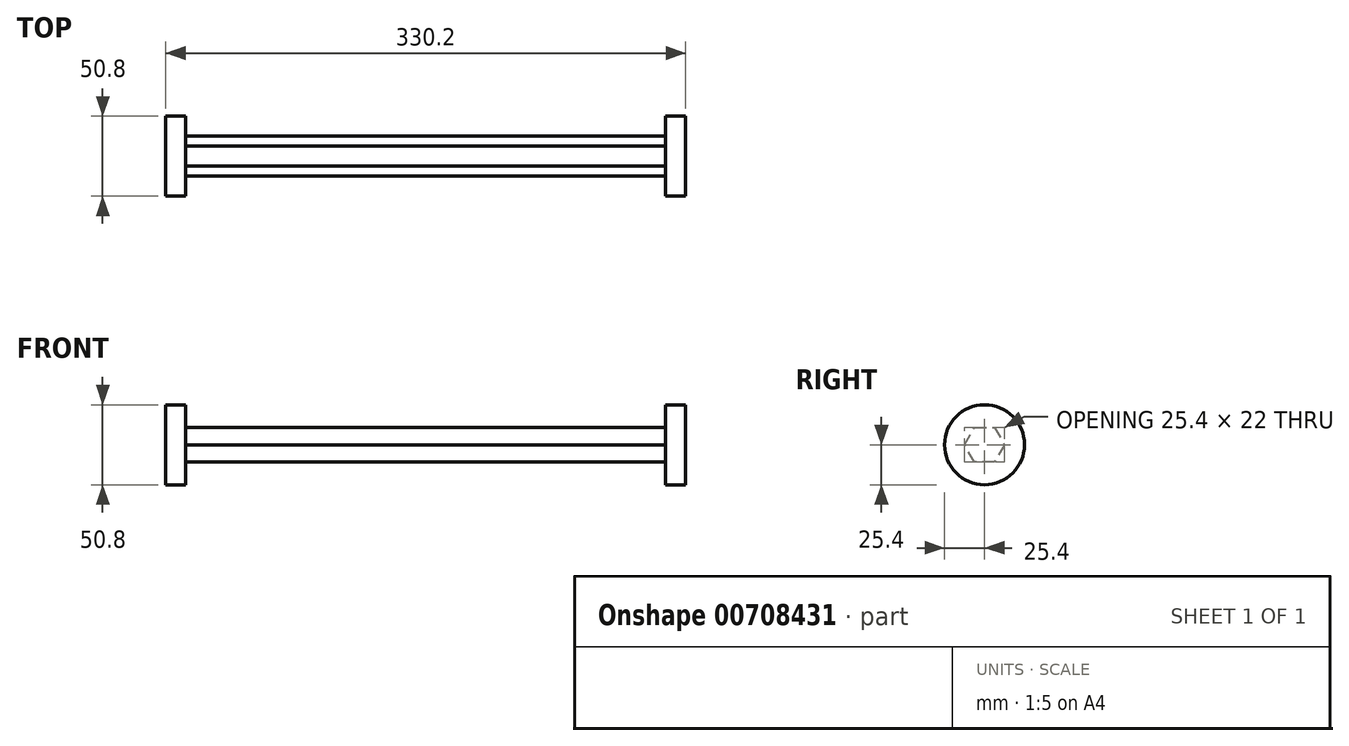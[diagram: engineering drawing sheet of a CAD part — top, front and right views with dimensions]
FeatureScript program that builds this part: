
annotation { "Feature Type Name" : "Feature", "Feature Type Description" : "" }
export const myFeature = defineFeature(function(context is Context, id is Id, definition is map)
    precondition{}
    {
        {
            var Q0;
            Q0=qCreatedBy(makeId("Right.planeOp"),FACE);
            var sketch = newSketch(context, id + "F0", { "sketchPlane" : qUnion([Q0])});
            skCircle(sketch, "E0.cCircle", {"center": v(0, 0) * mm, "radius": 12.7 * mm, "construction": true});
            skLineSegment(sketch, "E0.0", {"start": v(12.7, 0) * mm, "end": v(6.35, -11) * mm});
            skLineSegment(sketch, "E0.1", {"start": v(6.35, -11) * mm, "end": v(-6.35, -11) * mm});
            skLineSegment(sketch, "E0.2", {"start": v(-6.35, -11) * mm, "end": v(-12.7, 0) * mm});
            skLineSegment(sketch, "E0.3", {"start": v(-12.7, 0) * mm, "end": v(-6.35, 11) * mm});
            skLineSegment(sketch, "E0.4", {"start": v(-6.35, 11) * mm, "end": v(6.35, 11) * mm});
            skLineSegment(sketch, "E0.5", {"start": v(6.35, 11) * mm, "end": v(12.7, 0) * mm});
            skSolve(sketch);
        }
        {
            var Q0;
            Q0=makeQuery(id+"F0.imprint","IMPRINT",FACE,{"disambiguationData":[TD([[makeQuery(id+"F0.imprint","IMPRINT",EDGE,{"derivedFrom":sQuery(id+"F0.wireOp",EDGE,"E0.0")}),-1.0]])]});
            extrude(context, id + "F1", {"entities" : qUnion([Q0]), "depth" : 304.8 * mm, "offsetDistance" : 25.4 * mm});
        }
        {
            var Q0;
            Q0=makeQuery(id+"F1.opExtrude","CAP_FACE",FACE,{"disambiguationData":[OSD([sQuery(id+"F0.wireOp",EDGE,"E0.0"),sQuery(id+"F0.wireOp",EDGE,"E0.1"),sQuery(id+"F0.wireOp",EDGE,"E0.2"),sQuery(id+"F0.wireOp",EDGE,"E0.3"),sQuery(id+"F0.wireOp",EDGE,"E0.4"),sQuery(id+"F0.wireOp",EDGE,"E0.5")])],"isStart":false});
            var sketch = newSketch(context, id + "F2", { "sketchPlane" : qUnion([Q0])});
            skCircle(sketch, "E1", {"center": v(0, 0) * mm, "radius": 25.4 * mm});
            skSolve(sketch);
        }
        {
            var Q0;
            Q0=makeQuery(id+"F2.imprint","IMPRINT",FACE,{"disambiguationData":[TD([[makeQuery(id+"F2.imprint","IMPRINT",EDGE,{"derivedFrom":sQuery(id+"F2.wireOp",EDGE,"E1")}),1.0]])]});
            var Q1;
            Q1=makeQuery(id+"F2.imprint","IMPRINT",FACE,{"disambiguationData":[TD([[makeQuery(id+"F2.imprint","IMPRINT",EDGE,{"derivedFrom":makeQuery(id+"F1.opExtrude","CAP_EDGE",EDGE,{"disambiguationData":[OSD([sQuery(id+"F0.wireOp",EDGE,"E0.0")])],"isStart":false})}),-1.0]])]});
            extrude(context, id + "F3", {"entities" : qUnion([Q0, Q1]), "operationType" : NewBodyOperationType.ADD, "depth" : 12.7 * mm, "offsetDistance" : 25.4 * mm});
        }
        {
            var Q0;
            Q0=makeQuery(id+"F1.opExtrude","CAP_FACE",FACE,{"disambiguationData":[OSD([sQuery(id+"F0.wireOp",EDGE,"E0.0"),sQuery(id+"F0.wireOp",EDGE,"E0.1"),sQuery(id+"F0.wireOp",EDGE,"E0.2"),sQuery(id+"F0.wireOp",EDGE,"E0.3"),sQuery(id+"F0.wireOp",EDGE,"E0.4"),sQuery(id+"F0.wireOp",EDGE,"E0.5")])],"isStart":true});
            var sketch = newSketch(context, id + "F4", { "sketchPlane" : qUnion([Q0])});
            skCircle(sketch, "E2", {"center": v(0, 0) * mm, "radius": 25.4 * mm});
            skSolve(sketch);
        }
        {
            var Q0;
            Q0=makeQuery(id+"F4.imprint","IMPRINT",FACE,{"disambiguationData":[TD([[makeQuery(id+"F4.imprint","IMPRINT",EDGE,{"derivedFrom":sQuery(id+"F4.wireOp",EDGE,"E2")}),1.0]])]});
            var Q1;
            Q1=makeQuery(id+"F4.imprint","IMPRINT",FACE,{"disambiguationData":[TD([[makeQuery(id+"F4.imprint","IMPRINT",EDGE,{"derivedFrom":makeQuery(id+"F1.opExtrude","CAP_EDGE",EDGE,{"disambiguationData":[OSD([sQuery(id+"F0.wireOp",EDGE,"E0.0")])],"isStart":true})}),1.0]])]});
            extrude(context, id + "F5", {"entities" : qUnion([Q0, Q1]), "operationType" : NewBodyOperationType.ADD, "depth" : 12.7 * mm, "offsetDistance" : 25.4 * mm});
        }
    });
